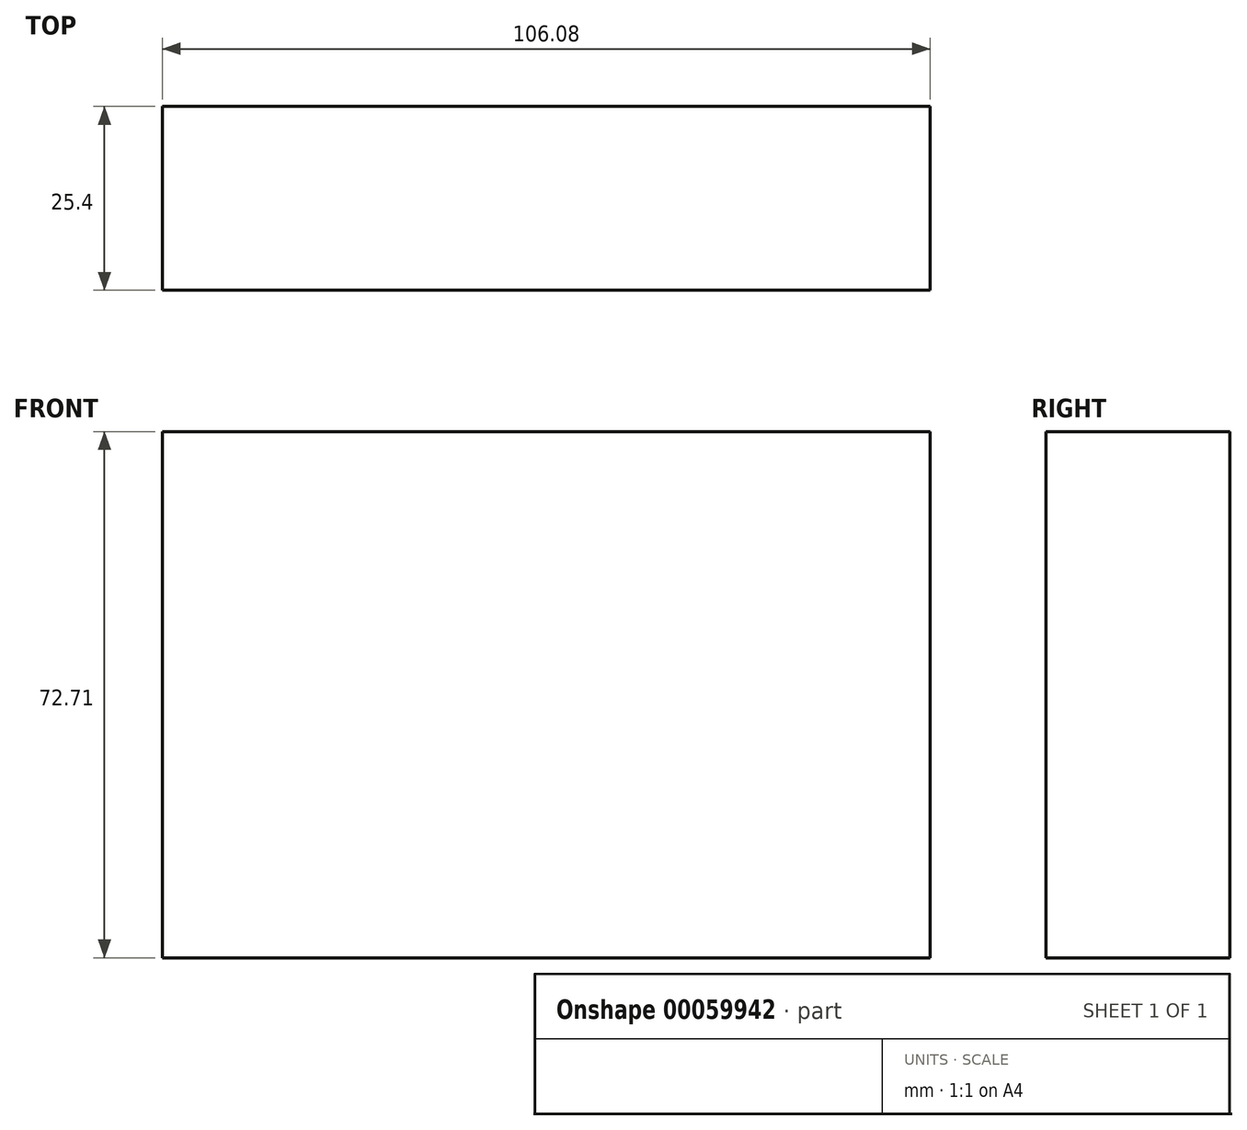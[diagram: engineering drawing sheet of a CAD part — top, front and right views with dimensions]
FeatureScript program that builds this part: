
annotation { "Feature Type Name" : "Feature", "Feature Type Description" : "" }
export const myFeature = defineFeature(function(context is Context, id is Id, definition is map)
    precondition{}
    {
        {
            var Q0;
            Q0=qCreatedBy(makeId("Front.planeOp"),FACE);
            var sketch = newSketch(context, id + "F0", { "sketchPlane" : qUnion([Q0])});
            skLineSegment(sketch, "E0.bottom", {"start": v(-51.25, 38.59) * mm, "end": v(54.83, 38.59) * mm});
            skLineSegment(sketch, "E0.top", {"start": v(-51.25, -34.12) * mm, "end": v(54.83, -34.12) * mm});
            skLineSegment(sketch, "E0.left", {"start": v(-51.25, 38.59) * mm, "end": v(-51.25, -34.12) * mm});
            skLineSegment(sketch, "E0.right", {"start": v(54.83, 38.59) * mm, "end": v(54.83, -34.12) * mm});
            skSolve(sketch);
        }
        {
            var Q0;
            Q0=makeQuery(id+"F0.imprint","IMPRINT",FACE,{"disambiguationData":[TD([[makeQuery(id+"F0.imprint","IMPRINT",EDGE,{"derivedFrom":sQuery(id+"F0.wireOp",EDGE,"E0.bottom")}),-1.0]])]});
            extrude(context, id + "F1", {"entities" : qUnion([Q0]), "endBound" : BoundingType.SYMMETRIC, "depth" : 25.4 * mm});
        }
    });
